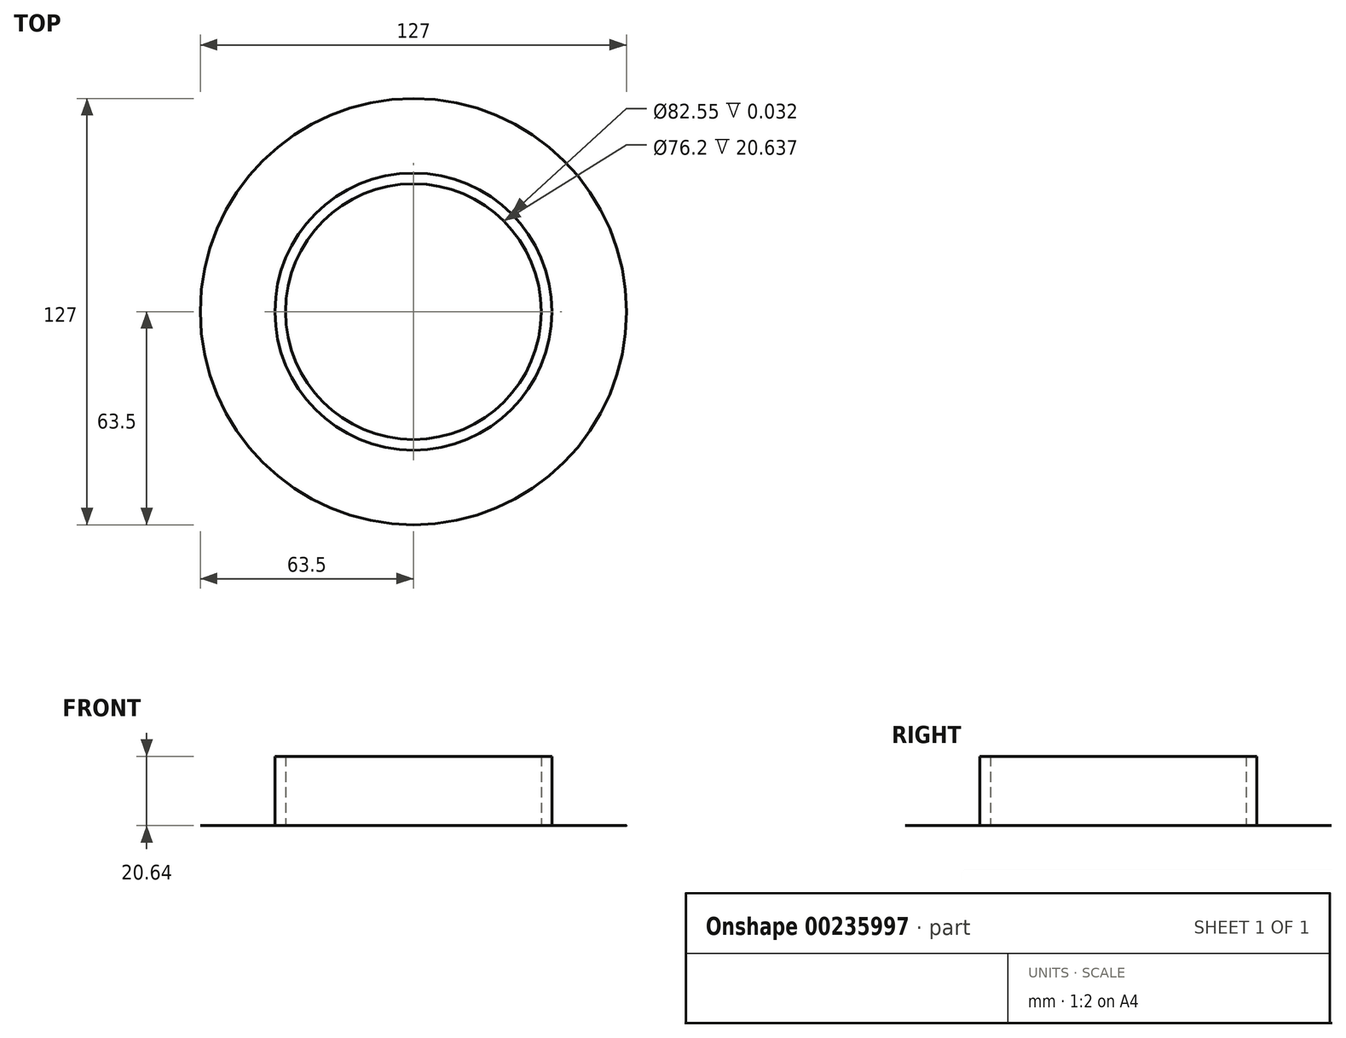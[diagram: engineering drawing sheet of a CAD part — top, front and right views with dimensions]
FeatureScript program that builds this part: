
annotation { "Feature Type Name" : "Feature", "Feature Type Description" : "" }
export const myFeature = defineFeature(function(context is Context, id is Id, definition is map)
    precondition{}
    {
        {
            var Q0;
            Q0=qCreatedBy(makeId("Top.planeOp"),FACE);
            var sketch = newSketch(context, id + "F0", { "sketchPlane" : qUnion([Q0])});
            skCircle(sketch, "E0", {"center": v(0, 0) * mm, "radius": 38.1 * mm});
            skCircle(sketch, "E1", {"center": v(0, 0) * mm, "radius": 41.28 * mm});
            skSolve(sketch);
        }
        {
            var Q0;
            Q0=makeQuery(id+"F0.imprint","IMPRINT",FACE,{"disambiguationData":[TD([[makeQuery(id+"F0.imprint","IMPRINT",EDGE,{"derivedFrom":sQuery(id+"F0.wireOp",EDGE,"E0")}),-1.0]])]});
            extrude(context, id + "F1", {"entities" : qUnion([Q0]), "depth" : 20.64 * mm});
        }
        {
            var Q0;
            Q0=qCreatedBy(makeId("Top.planeOp"),FACE);
            var sketch = newSketch(context, id + "F2", { "sketchPlane" : qUnion([Q0])});
            skCircle(sketch, "E2.0", {"center": v(0, 0) * mm, "radius": 41.28 * mm});
            skCircle(sketch, "E3.0", {"center": v(0, 0) * mm, "radius": 63.5 * mm});
            skSolve(sketch);
        }
        {
            var Q0;
            Q0 = qSketchRegion(id + "F2", true);
            extrude(context, id + "F3", {"entities" : qUnion([Q0]), "depth" : 13 / 406.4 * mm});
        }
    });
